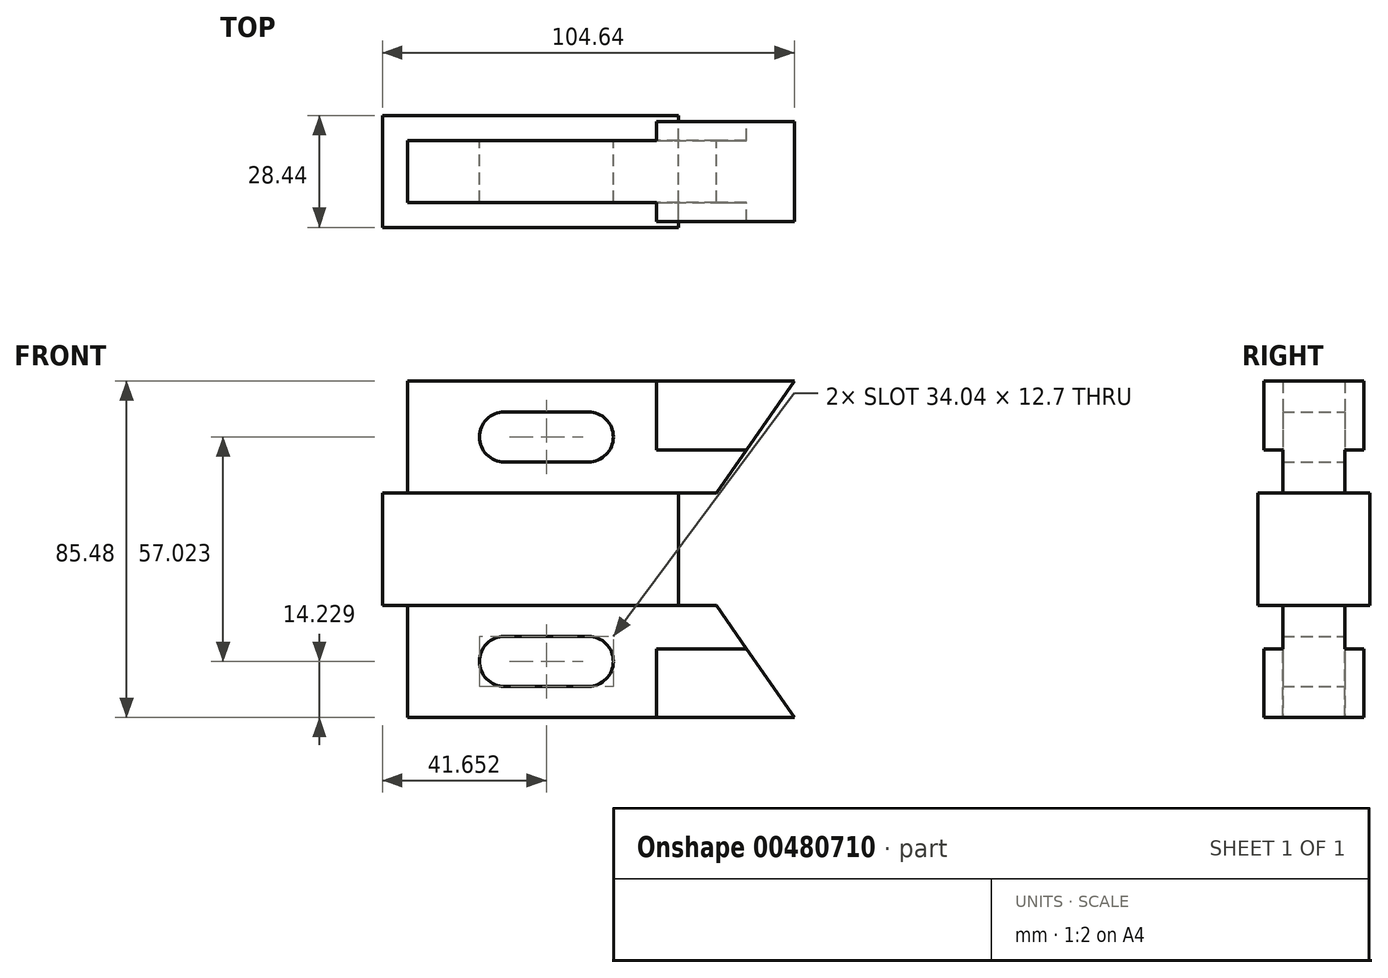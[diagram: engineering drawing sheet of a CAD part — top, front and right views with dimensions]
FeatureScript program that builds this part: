
annotation { "Feature Type Name" : "Feature", "Feature Type Description" : "" }
export const myFeature = defineFeature(function(context is Context, id is Id, definition is map)
    precondition{}
    {
        {
            var Q0;
            Q0=qCreatedBy(makeId("Front.planeOp"),FACE);
            var sketch = newSketch(context, id + "F0", { "sketchPlane" : qUnion([Q0])});
            skLineSegment(sketch, "E0.bottom", {"start": v(52.32, 42.74) * mm, "end": v(-52.32, 42.74) * mm});
            skLineSegment(sketch, "E0.top", {"start": v(52.32, -42.74) * mm, "end": v(-52.32, -42.74) * mm});
            skLineSegment(sketch, "E0.right", {"start": v(-52.32, 42.74) * mm, "end": v(-52.32, -42.74) * mm});
            skPoint(sketch, "E0.middle", {"position": v(0, 0) * mm});
            skLineSegment(sketch, "E1", {"start": v(52.32, 42.74) * mm, "end": v(32.52, 14.29) * mm});
            skLineSegment(sketch, "E2", {"start": v(32.52, 14.29) * mm, "end": v(22.96, 14.29) * mm});
            skLineSegment(sketch, "E3", {"start": v(22.96, 14.29) * mm, "end": v(22.96, -14.29) * mm});
            skLineSegment(sketch, "E4", {"start": v(22.96, -14.29) * mm, "end": v(32.52, -14.29) * mm});
            skLineSegment(sketch, "E5", {"start": v(32.52, -14.29) * mm, "end": v(52.32, -42.74) * mm});
            skLineSegment(sketch, "E6", {"start": v(22.96, 14.29) * mm, "end": v(-52.32, 14.29) * mm});
            skLineSegment(sketch, "E7", {"start": v(17.27, 42.74) * mm, "end": v(17.27, 25.2) * mm});
            skLineSegment(sketch, "E8", {"start": v(17.27, 25.2) * mm, "end": v(40.13, 25.2) * mm});
            skLineSegment(sketch, "E9", {"start": v(-45.97, 42.74) * mm, "end": v(-45.97, 14.29) * mm});
            skLineSegment(sketch, "E10", {"start": v(-21.34, 28.51) * mm, "end": v(0, 28.51) * mm, "construction": true});
            skPoint(sketch, "E10.startSnap0", {"position": v(-45.97, 28.51) * mm});
            skArc(sketch, "E11.0.startCap", {"start": v(-21.34, 22.16) * mm, "mid": v(-27.69, 28.51) * mm, "end": v(-21.34, 34.86) * mm});
            skArc(sketch, "E11.0.endCap", {"start": v(0, 34.86) * mm, "mid": v(6.35, 28.51) * mm, "end": v(0, 22.16) * mm});
            skLineSegment(sketch, "E11.0.left", {"start": v(-21.34, 34.86) * mm, "end": v(0, 34.86) * mm});
            skLineSegment(sketch, "E11.0.right", {"start": v(-21.34, 22.16) * mm, "end": v(0, 22.16) * mm});
            skLineSegment(sketch, "E12.MirrorCS", {"start": v(17.27, -42.9) * mm, "end": v(17.27, -25.37) * mm});
            skLineSegment(sketch, "E13", {"start": v(22.96, -14.29) * mm, "end": v(-52.32, -14.29) * mm});
            skLineSegment(sketch, "E14", {"start": v(-52.32, 0) * mm, "end": v(22.96, 0) * mm, "construction": true});
            skLineSegment(sketch, "E15", {"start": v(17.27, -25.37) * mm, "end": v(40.23, -25.37) * mm});
            skLineSegment(sketch, "E16", {"start": v(-45.97, -14.29) * mm, "end": v(-45.97, -42.74) * mm});
            skLineSegment(sketch, "E17.MirrorCS", {"start": v(-21.34, -28.51) * mm, "end": v(0, -28.51) * mm, "construction": true});
            skArc(sketch, "E18.0.startCap", {"start": v(-21.34, -34.86) * mm, "mid": v(-27.69, -28.51) * mm, "end": v(-21.34, -22.16) * mm});
            skArc(sketch, "E18.0.endCap", {"start": v(0, -22.16) * mm, "mid": v(6.35, -28.51) * mm, "end": v(0, -34.86) * mm});
            skLineSegment(sketch, "E18.0.left", {"start": v(-21.34, -22.16) * mm, "end": v(0, -22.16) * mm});
            skLineSegment(sketch, "E18.0.right", {"start": v(-21.34, -34.86) * mm, "end": v(0, -34.86) * mm});
            skSolve(sketch);
        }
        {
            var Q0;
            {var subQ1=sQuery(id+"F0.wireOp",EDGE,"E3");Q0=makeQuery(id+"F0.imprint","IMPRINT",FACE,{"disambiguationData":[TD([[makeQuery(id+"F0.imprint","IMPRINT",EDGE,{"derivedFrom":subQ1}),-1.0]])]});}
            extrude(context, id + "F1", {"entities" : qUnion([Q0]), "endBound" : BoundingType.SYMMETRIC, "depth" : 28.45 * mm, "offsetDistance" : 25.4 * mm});
        }
        {
            var Q0;
            {var subQ4=sQuery(id+"F0.wireOp",EDGE,"E2");Q0=makeQuery(id+"F0.imprint","IMPRINT",FACE,{"disambiguationData":[TD([[makeQuery(id+"F0.imprint","IMPRINT",EDGE,{"derivedFrom":subQ4}),-1.0]])]});}
            var Q1;
            {var subQ3=sQuery(id+"F0.wireOp",EDGE,"E4");Q1=makeQuery(id+"F0.imprint","IMPRINT",FACE,{"disambiguationData":[TD([[makeQuery(id+"F0.imprint","IMPRINT",EDGE,{"derivedFrom":subQ3}),-1.0]])]});}
            extrude(context, id + "F2", {"entities" : qUnion([Q0, Q1]), "operationType" : NewBodyOperationType.ADD, "endBound" : BoundingType.SYMMETRIC, "depth" : 15.75 * mm, "offsetDistance" : 25.4 * mm});
        }
        {
            var Q0;
            {var subQ3=sQuery(id+"F0.wireOp",EDGE,"E7");Q0=makeQuery(id+"F0.imprint","IMPRINT",FACE,{"disambiguationData":[TD([[makeQuery(id+"F0.imprint","IMPRINT",EDGE,{"derivedFrom":subQ3}),1.0]])]});}
            var Q1;
            {var subQ5=sQuery(id+"F0.wireOp",EDGE,"E15");Q1=makeQuery(id+"F0.imprint","IMPRINT",FACE,{"disambiguationData":[TD([[makeQuery(id+"F0.imprint","IMPRINT",EDGE,{"derivedFrom":subQ5}),-1.0]])]});}
            extrude(context, id + "F3", {"entities" : qUnion([Q0, Q1]), "operationType" : NewBodyOperationType.ADD, "endBound" : BoundingType.SYMMETRIC, "depth" : 25.4 * mm, "offsetDistance" : 25.4 * mm});
        }
    });
